# Revit family: ShowerBase_ProSlopeExtension_NobleCompany
name_source: partatom
category: Specialty Equipment
revit_build: Autodesk Revit 2015 (Build: 20140606_1530(x64)
units: mm (PartAtom-declared; Revit-internal decimal feet)

## types (4) — shared parameters
Assembly Code = D2030300
Base = Polymer coated Expanded Polystyrene
Building Codes = http://www.noblecompany.com
Default Elevation = 0"
Description = Noble Pro Slope Shower Base
Drain Hole Diameter = 3"
Hang = 1/8"
Height = 1 7/8"
Installation-Fabrication = http://www.noblecompany.com
Manufacturer = Noble Company
Manufacturer Fax = 231-799-8850
Model = Pro Slope
Panel Size = 16"
Product Data = http://www.noblecompany.com
Product Properties = http://www.noblecompany.com
URL = www.noblecompany.com

## per-type parameters (varying)
| type | Depth | Flat | MinThick | Tapered | Width |
| 20x40 Flat | 20" | Yes | 1" | No | 40" |
| 30x60 Flat | 30" | Yes | 1 1/4" | No | 60" |
| 30x60 Tapered | 30" | No | 1 1/4" | Yes | 60" |
| 20x40 Tapered | 20" | No | 1" | Yes | 40" |

## geometry (parser evidence)
native form markers: Sweep x2
no freeform markers — native parametric forms only
